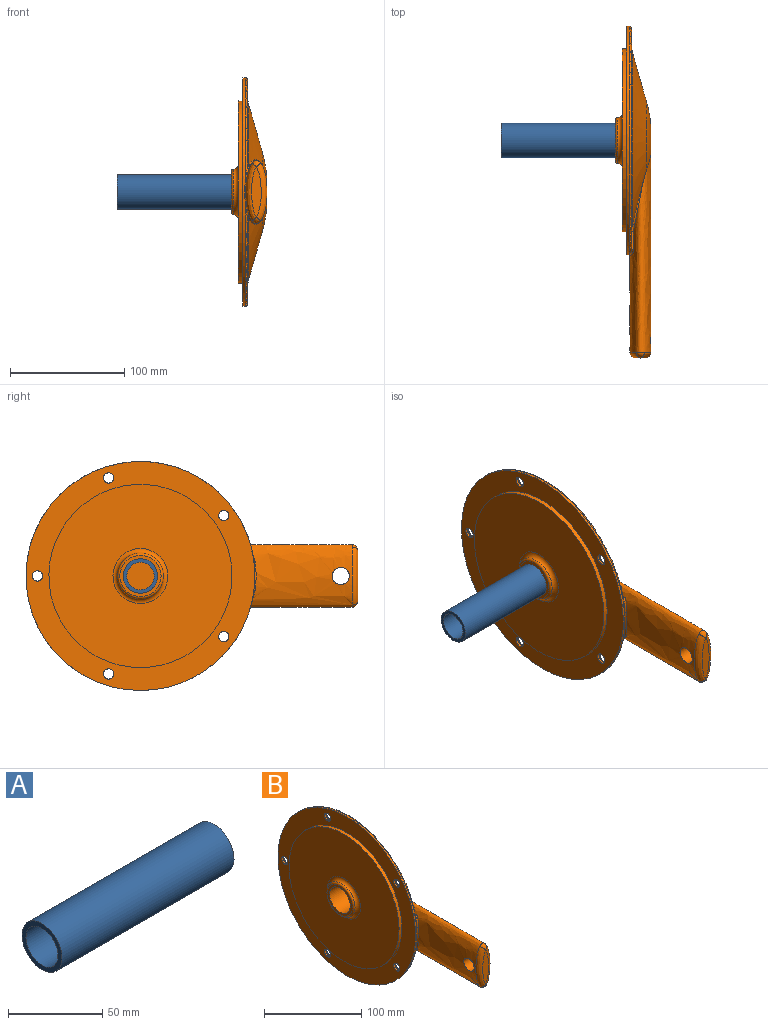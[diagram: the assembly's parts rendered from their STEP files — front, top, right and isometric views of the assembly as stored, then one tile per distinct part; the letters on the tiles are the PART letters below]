
ASSEMBLY  parts=2 mates=1
PART A: 4 faces, bbox 129x30x30 mm
  f0: plane 30x30mm, normal (-1,0,0), area 254.5mm2, adj f1,f3
  f1: cylinder r=12mm len=129mm, axis (-1,0,0), area 9726.4mm2, adj f0,f2
  f2: plane 30x30mm, normal (1,0,0), area 254.5mm2, adj f1,f3
  f3: cylinder r=15mm len=129mm, axis (-1,0,0), area 12158mm2, adj f0,f2
PART B: 63 faces, bbox 39.8x306.2x224.5 mm
  f0: extruded ~178.89x55mm, area 15583.5mm2, adj f1,f2,f3,f5,f6,f52,f53,f54
  f1: cylinder r=7.5mm len=17.8mm, axis (-1,0,0), area 838.7mm2, adj f0
  f2: bspline ~7.15x5.71mm, area 27.4mm2, adj f0,f3,f62
  f3: bspline ~51.11x9.66mm, area 388.8mm2, adj f0,f2,f4,f5
  f4: plane 43.58x8.51mm, normal (0,-1,0), area 265.1mm2, adj f3,f62
  f5: bspline ~7.14x5.71mm, area 42.8mm2, adj f0,f3,f62
  f6: bspline ~24.55x22.12mm, area 2.7mm2, adj f0,f7,f61
  f7: torus R=6.11mm, axis (-1,0,0), area 2730.8mm2, adj f6,f8,f51,f52
  f8: cone r=80mm half-angle=74.2deg, axis (-1,0,0), area 13408mm2, adj f7,f9,f53,f61
  f9: torus R=82.78mm, axis (-1,0,0), area 2524.7mm2, adj f8,f10,f54,f60
  f10: plane 204x201.56mm, normal (1,0,0), area 7501mm2, adj f9,f11,f45,f46,f47,f48,f49,f50
  f11: torus R=98mm, axis (-1,0,0), area 36.6mm2, adj f10,f12,f58
  f12: cylinder r=100mm len=200mm, axis (1,0,0), area 1256.6mm2, adj f11,f13,f45,f57
  f13: plane 200x200mm, normal (-1,0,0), area 10991.6mm2, adj f12,f14,f35,f37,f39,f41,f43
  f14: cylinder r=80mm len=160mm, axis (1,0,0), area 2010.6mm2, adj f13,f15
  f15: plane 160x160mm, normal (-1,0,0), area 18296.6mm2, adj f14,f16
  f16: torus R=24mm, axis (1,0,0), area 847mm2, adj f15,f17
  f17: torus R=18mm, axis (-1,0,0), area 380.4mm2, adj f16,f18
  f18: plane 36x36mm, normal (-1,0,0), area 311mm2, adj f17,f19
  f19: cylinder r=15mm len=30mm, axis (-1,0,0), area 2103.7mm2, adj f18,f20,f29,f30,f31,f33,f34
  f20: plane 11.41x5.03mm, normal (0,-1,0), area 50.2mm2, adj f19,f21,f28,f31,f34
  f21: torus R=22.5mm, axis (-1,0,0), area 449.7mm2, adj f20,f22,f28,f31,f33
  f22: cone r=74.18mm half-angle=74.2deg, axis (-1,0,0), area 14081.7mm2, adj f21,f23,f31
  f23: torus R=73.5mm, axis (-1,0,0), area 1532.6mm2, adj f22,f24
  f24: cylinder r=76mm len=152mm, axis (-1,0,0), area 317.3mm2, adj f23,f25
  f25: torus R=73.5mm, axis (-1,0,0), area 1852.8mm2, adj f24,f26
  f26: plane 147x147mm, normal (1,0,0), area 15381.2mm2, adj f25,f27
  f27: torus R=22.5mm, axis (-1,0,0), area 515.9mm2, adj f26,f28
  f28: cylinder r=20mm len=40mm, axis (-1,0,0), area 1391.6mm2, adj f20,f21,f27,f33,f34
  f29: cylinder r=15mm len=15mm, axis (-1,0,0), area 18.2mm2, adj f19,f30,f31
  f30: plane 30x30mm, normal (-1,0,0), area 706.9mm2, adj f19,f29
  f31: extruded ~160x51mm, area 13342.2mm2, adj f19,f20,f21,f22,f29,f32,f33
  f32: plane 51x14.5mm, normal (0,1,0), area 566.4mm2, adj f31
  f33: plane 11.41x5.03mm, normal (0,-1,0), area 50.2mm2, adj f19,f21,f28,f31,f34
  f34: extruded ~40x20mm, area 280.1mm2, adj f19,f20,f28,f33
  f35: cylinder r=4.5mm len=9mm, axis (1,0,0), area 56.5mm2, adj f13,f36
  f36: plane 11x11mm, normal (1,0,0), area 31.4mm2, adj f35,f46
  f37: cylinder r=4.5mm len=9mm, axis (1,0,0), area 56.5mm2, adj f13,f38
  f38: plane 11x11mm, normal (1,0,0), area 31.4mm2, adj f37,f47
  f39: cylinder r=4.5mm len=9mm, axis (1,0,0), area 56.5mm2, adj f13,f40
  f40: plane 11x11mm, normal (1,0,0), area 31.4mm2, adj f39,f48
  f41: cylinder r=4.5mm len=9mm, axis (1,0,0), area 56.5mm2, adj f13,f42
  f42: plane 11x11mm, normal (1,0,0), area 31.4mm2, adj f41,f49
  f43: cylinder r=4.5mm len=9mm, axis (1,0,0), area 56.5mm2, adj f13,f44
  f44: plane 11x11mm, normal (1,0,0), area 31.4mm2, adj f43,f50
  f45: torus R=98mm, axis (-1,0,0), area 2955.1mm2, adj f10,f12,f56
  f46: cylinder r=5.5mm len=11mm, axis (1,0,0), area 69.1mm2, adj f10,f36
  f47: cylinder r=5.5mm len=11mm, axis (1,0,0), area 69.1mm2, adj f10,f38
  f48: cylinder r=5.5mm len=11mm, axis (1,0,0), area 69.1mm2, adj f10,f40
  f49: cylinder r=5.5mm len=11mm, axis (1,0,0), area 69.1mm2, adj f10,f42
  f50: cylinder r=5.5mm len=11mm, axis (1,0,0), area 69.1mm2, adj f10,f44
  f51: plane 12.21x12.21mm, normal (1,0,0), area 117.2mm2, adj f7
  f52: bspline ~23.6x20.66mm, area 2.7mm2, adj f0,f7,f53
  f53: bspline ~53.97x13.94mm, area 75mm2, adj f0,f8,f52,f54
  f54: bspline ~11.04x7.17mm, area 17.3mm2, adj f0,f9,f53,f55
  f55: cylinder r=1mm len=15.69mm, axis (0,1,0), area 43.1mm2, adj f0,f10,f54,f56
  f56: bspline ~13.74x6.33mm, area 27mm2, adj f0,f45,f55,f57
  f57: bspline ~23.47x2.09mm, area 27.8mm2, adj f0,f12,f56,f58
  f58: bspline ~15.2x6.42mm, area 27mm2, adj f0,f11,f57,f59
  f59: cylinder r=1mm len=15.69mm, axis (0,1,0), area 43.1mm2, adj f0,f10,f58,f60
  f60: bspline ~11.2x7.26mm, area 17.3mm2, adj f0,f9,f59,f61
  f61: bspline ~53.42x13.52mm, area 75mm2, adj f0,f6,f8,f60
  f62: bspline ~51.43x9.74mm, area 388.7mm2, adj f0,f2,f4,f5
PLACE A t=(-35.5,0,0)mm
PLACE B at identity fixed
MATE fastened A.f1 <-> B.f19  axis (-1,0,0) through (29,0,0)mm
